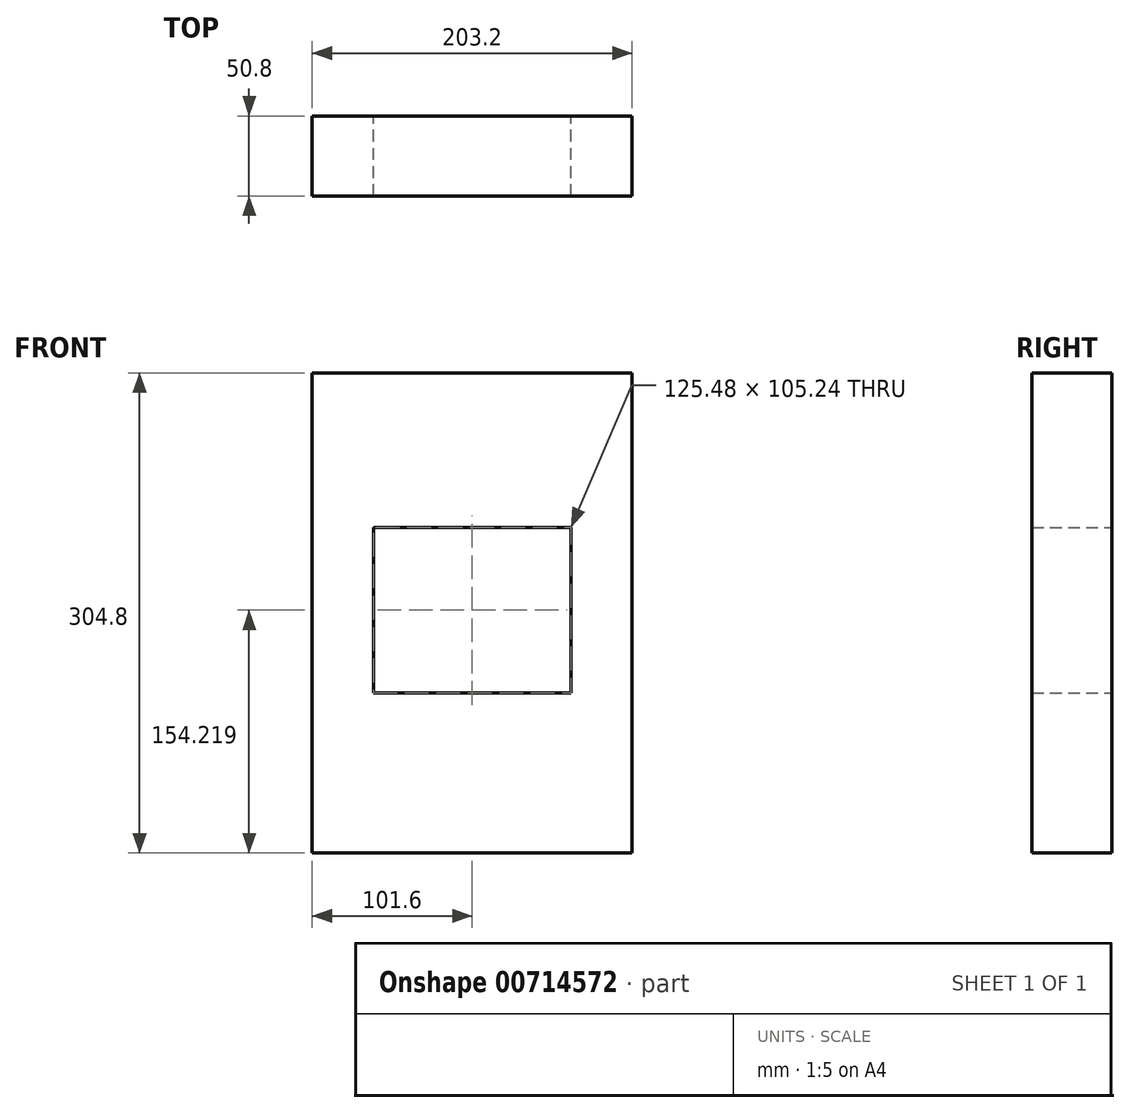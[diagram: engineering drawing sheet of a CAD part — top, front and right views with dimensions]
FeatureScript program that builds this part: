
annotation { "Feature Type Name" : "Feature", "Feature Type Description" : "" }
export const myFeature = defineFeature(function(context is Context, id is Id, definition is map)
    precondition{}
    {
        {
            var Q0;
            Q0=qCreatedBy(makeId("Front.planeOp"),FACE);
            var sketch = newSketch(context, id + "F0", { "sketchPlane" : qUnion([Q0])});
            skLineSegment(sketch, "E0.bottom", {"start": v(-101.6, 152.4) * mm, "end": v(101.6, 152.4) * mm});
            skLineSegment(sketch, "E0.top", {"start": v(-101.6, -152.4) * mm, "end": v(101.6, -152.4) * mm});
            skLineSegment(sketch, "E0.left", {"start": v(-101.6, 152.4) * mm, "end": v(-101.6, -152.4) * mm});
            skLineSegment(sketch, "E0.right", {"start": v(101.6, 152.4) * mm, "end": v(101.6, -152.4) * mm});
            skLineSegment(sketch, "E1.bottom", {"start": v(-38.86, -50.8) * mm, "end": v(38.86, -50.8) * mm});
            skLineSegment(sketch, "E1.top", {"start": v(-38.86, -109.74) * mm, "end": v(38.86, -109.74) * mm});
            skLineSegment(sketch, "E1.left", {"start": v(-38.86, -50.8) * mm, "end": v(-38.86, -109.74) * mm});
            skLineSegment(sketch, "E1.right", {"start": v(38.86, -50.8) * mm, "end": v(38.86, -109.74) * mm});
            skLineSegment(sketch, "E2.bottom", {"start": v(-62.74, 114.3) * mm, "end": v(62.74, 114.3) * mm});
            skLineSegment(sketch, "E2.top", {"start": v(-62.74, 54.44) * mm, "end": v(62.74, 54.44) * mm});
            skLineSegment(sketch, "E2.left", {"start": v(-62.74, 114.3) * mm, "end": v(-62.74, 54.44) * mm});
            skLineSegment(sketch, "E2.right", {"start": v(62.74, 114.3) * mm, "end": v(62.74, 54.44) * mm});
            skLineSegment(sketch, "E3", {"start": v(62.74, 54.44) * mm, "end": v(62.74, -50.8) * mm});
            skLineSegment(sketch, "E4", {"start": v(62.74, -50.8) * mm, "end": v(-62.74, -50.8) * mm});
            skLineSegment(sketch, "E5", {"start": v(-62.74, 54.44) * mm, "end": v(-62.74, -50.8) * mm});
            skSolve(sketch);
        }
        {
            var Q0;
            Q0 = qSketchRegion(id + "F0", true);
            var Q1;
            Q1=makeQuery(id+"F0.imprint","IMPRINT",FACE,{"disambiguationData":[TD([[makeQuery(id+"F0.imprint","IMPRINT",EDGE,{"derivedFrom":sQuery(id+"F0.wireOp",EDGE,"E2.bottom")}),-1.0]])]});
            var Q2;
            Q2=makeQuery(id+"F0.imprint","IMPRINT",FACE,{"disambiguationData":[TD([[makeQuery(id+"F0.imprint","IMPRINT",EDGE,{"derivedFrom":sQuery(id+"F0.wireOp",EDGE,"E1.top")}),1.0]])]});
            extrude(context, id + "F1", {"entities" : qUnion([Q0, Q1, Q2]), "depth" : 50.8 * mm, "offsetDistance" : 25.4 * mm});
        }
    });
